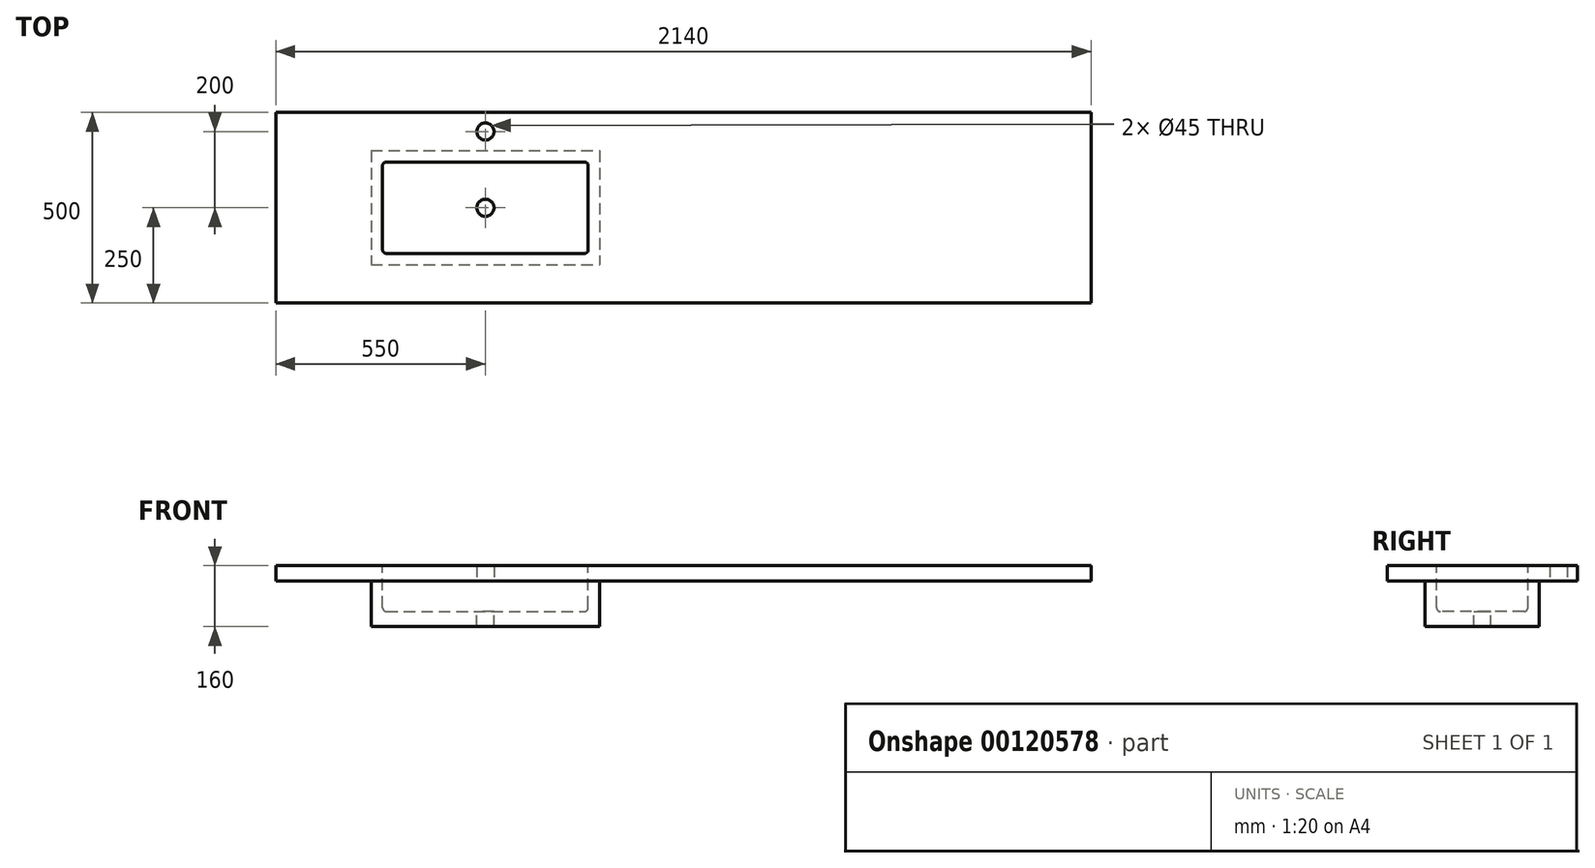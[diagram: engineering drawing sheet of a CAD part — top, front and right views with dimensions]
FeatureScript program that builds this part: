
annotation { "Feature Type Name" : "Feature", "Feature Type Description" : "" }
export const myFeature = defineFeature(function(context is Context, id is Id, definition is map)
    precondition{}
    {
        {
            var Q0;
            Q0=qCreatedBy(makeId("Top.planeOp"),FACE);
            var sketch = newSketch(context, id + "F0", { "sketchPlane" : qUnion([Q0])});
            skLineSegment(sketch, "E0.bottom", {"start": v(1070, 250) * mm, "end": v(-1070, 250) * mm});
            skLineSegment(sketch, "E0.top", {"start": v(1070, -250) * mm, "end": v(-1070, -250) * mm});
            skLineSegment(sketch, "E0.left", {"start": v(1070, 250) * mm, "end": v(1070, -250) * mm});
            skLineSegment(sketch, "E0.right", {"start": v(-1070, 250) * mm, "end": v(-1070, -250) * mm});
            skPoint(sketch, "E0.middle", {"position": v(0, 0) * mm});
            skSolve(sketch);
        }
        {
            var Q0;
            Q0 = qSketchRegion(id + "F0", true);
            extrude(context, id + "F1", {"entities" : qUnion([Q0]), "depth" : 40 * mm, "offsetDistance" : 25 * mm});
        }
        {
            var Q0;
            Q0=makeQuery(id+"F1.opExtrude","CAP_FACE",FACE,{"disambiguationData":[OSD([sQuery(id+"F0.wireOp",EDGE,"E0.bottom"),sQuery(id+"F0.wireOp",EDGE,"E0.top"),sQuery(id+"F0.wireOp",EDGE,"E0.left"),sQuery(id+"F0.wireOp",EDGE,"E0.right")])],"isStart":true});
            var sketch = newSketch(context, id + "F2", { "sketchPlane" : qUnion([Q0])});
            skLineSegment(sketch, "E1.bottom", {"start": v(-820, -150) * mm, "end": v(-220, -150) * mm});
            skLineSegment(sketch, "E1.top", {"start": v(-820, 150) * mm, "end": v(-220, 150) * mm});
            skLineSegment(sketch, "E1.left", {"start": v(-820, -150) * mm, "end": v(-820, 150) * mm});
            skLineSegment(sketch, "E1.right", {"start": v(-220, -150) * mm, "end": v(-220, 150) * mm});
            skLineSegment(sketch, "E2", {"start": v(-820, 0) * mm, "end": v(-1070, 0) * mm, "construction": true});
            skSolve(sketch);
        }
        {
            var Q0;
            Q0=makeQuery(id+"F2.imprint","IMPRINT",FACE,{"disambiguationData":[TD([[makeQuery(id+"F2.imprint","IMPRINT",EDGE,{"derivedFrom":sQuery(id+"F2.wireOp",EDGE,"E1.bottom")}),1.0]])]});
            extrude(context, id + "F3", {"entities" : qUnion([Q0]), "operationType" : NewBodyOperationType.ADD, "depth" : 120 * mm, "offsetDistance" : 25 * mm});
        }
        {
            var Q0;
            Q0=makeQuery(id+"F1.opExtrude","CAP_FACE",FACE,{"disambiguationData":[OSD([sQuery(id+"F0.wireOp",EDGE,"E0.bottom"),sQuery(id+"F0.wireOp",EDGE,"E0.top"),sQuery(id+"F0.wireOp",EDGE,"E0.left"),sQuery(id+"F0.wireOp",EDGE,"E0.right")])],"isStart":true});
            var sketch = newSketch(context, id + "F4", { "sketchPlane" : qUnion([Q0])});
            skCircle(sketch, "E3", {"center": v(-520, -200) * mm, "radius": 20 * mm});
            skLineSegment(sketch, "E4", {"start": v(-520, -200) * mm, "end": v(-520, -150) * mm});
            skSolve(sketch);
        }
        {
            var Q0;
            Q0=sQuery(id+"F4.wireOp",VERTEX,"E3.center");
            var Q1;
            Q1=makeQuery(id+"F1.opExtrude","SWEPT_BODY",BODY,{"disambiguationData":[OSD([sQuery(id+"F0.wireOp",EDGE,"E0.bottom"),sQuery(id+"F0.wireOp",EDGE,"E0.top"),sQuery(id+"F0.wireOp",EDGE,"E0.left"),sQuery(id+"F0.wireOp",EDGE,"E0.right")])]});
            hole(context, id + "F5", {"style" : HoleStyle.SIMPLE, "endStyle" : HoleEndStyle.THROUGH, "holeDiameter" : 45 * mm, "locations" : qUnion([Q0]), "scope" : qUnion([Q1]), "majorDiameter" : 5 * mm, "tappedDepth" : 12 * mm, "tapClearance" : 3});
        }
        {
            var Q0;
            Q0=makeQuery(id+"F1.opExtrude","CAP_FACE",FACE,{"disambiguationData":[OSD([sQuery(id+"F0.wireOp",EDGE,"E0.bottom"),sQuery(id+"F0.wireOp",EDGE,"E0.top"),sQuery(id+"F0.wireOp",EDGE,"E0.left"),sQuery(id+"F0.wireOp",EDGE,"E0.right")])],"isStart":false});
            var sketch = newSketch(context, id + "F6", { "sketchPlane" : qUnion([Q0])});
            skLineSegment(sketch, "E5.0.0", {"start": v(-220, -150) * mm, "end": v(-820, -150) * mm});
            skLineSegment(sketch, "E5.0.1", {"start": v(-820, -150) * mm, "end": v(-820, 150) * mm});
            skLineSegment(sketch, "E5.0.2", {"start": v(-820, 150) * mm, "end": v(-220, 150) * mm});
            skLineSegment(sketch, "E5.0.3", {"start": v(-220, 150) * mm, "end": v(-220, -150) * mm});
            skLineSegment(sketch, "E6.0", {"start": v(-250, -120) * mm, "end": v(-790, -120) * mm});
            skLineSegment(sketch, "E6.1", {"start": v(-250, 120) * mm, "end": v(-250, -120) * mm});
            skLineSegment(sketch, "E6.2", {"start": v(-790, 120) * mm, "end": v(-250, 120) * mm});
            skLineSegment(sketch, "E6.3", {"start": v(-790, -120) * mm, "end": v(-790, 120) * mm});
            skSolve(sketch);
        }
        {
            var Q0;
            Q0=makeQuery(id+"F6.imprint","IMPRINT",FACE,{"disambiguationData":[TD([[makeQuery(id+"F6.imprint","IMPRINT",EDGE,{"derivedFrom":sQuery(id+"F6.wireOp",EDGE,"E6.0")}),-1.0]])]});
            extrude(context, id + "F7", {"entities" : qUnion([Q0]), "operationType" : NewBodyOperationType.REMOVE, "oppositeDirection" : true, "depth" : 120 * mm, "offsetDistance" : 25 * mm});
        }
        {
            var Q0;
            Q0=makeQuery(id+"F7.boolean.opBoolean","COPY",EDGE,{"derivedFrom":makeQuery(id+"F7.opExtrude","SWEPT_EDGE",EDGE,{"disambiguationData":[OSD([sQuery(id+"F6.wireOp",EDGE,"E6.0"),sQuery(id+"F6.wireOp",EDGE,"E6.1")])]})});
            var Q1;
            Q1=makeQuery(id+"F7.boolean.opBoolean","COPY",EDGE,{"derivedFrom":makeQuery(id+"F7.opExtrude","CAP_EDGE",EDGE,{"disambiguationData":[OSD([sQuery(id+"F6.wireOp",EDGE,"E6.1")])],"isStart":false})});
            var Q2;
            Q2=makeQuery(id+"F7.boolean.opBoolean","COPY",EDGE,{"derivedFrom":makeQuery(id+"F7.opExtrude","CAP_EDGE",EDGE,{"disambiguationData":[OSD([sQuery(id+"F6.wireOp",EDGE,"E6.0")])],"isStart":false})});
            var Q3;
            Q3=makeQuery(id+"F7.boolean.opBoolean","COPY",EDGE,{"derivedFrom":makeQuery(id+"F7.opExtrude","SWEPT_EDGE",EDGE,{"disambiguationData":[OSD([sQuery(id+"F6.wireOp",EDGE,"E6.0"),sQuery(id+"F6.wireOp",EDGE,"E6.3")])]})});
            var Q4;
            Q4=makeQuery(id+"F7.boolean.opBoolean","COPY",EDGE,{"derivedFrom":makeQuery(id+"F7.opExtrude","CAP_EDGE",EDGE,{"disambiguationData":[OSD([sQuery(id+"F6.wireOp",EDGE,"E6.3")])],"isStart":false})});
            var Q5;
            Q5=makeQuery(id+"F7.boolean.opBoolean","COPY",EDGE,{"derivedFrom":makeQuery(id+"F7.opExtrude","CAP_EDGE",EDGE,{"disambiguationData":[OSD([sQuery(id+"F6.wireOp",EDGE,"E6.2")])],"isStart":false})});
            var Q6;
            Q6=makeQuery(id+"F7.boolean.opBoolean","COPY",EDGE,{"derivedFrom":makeQuery(id+"F7.opExtrude","SWEPT_EDGE",EDGE,{"disambiguationData":[OSD([sQuery(id+"F6.wireOp",EDGE,"E6.1"),sQuery(id+"F6.wireOp",EDGE,"E6.2")])]})});
            var Q7;
            Q7=makeQuery(id+"F7.boolean.opBoolean","COPY",EDGE,{"derivedFrom":makeQuery(id+"F7.opExtrude","SWEPT_EDGE",EDGE,{"disambiguationData":[OSD([sQuery(id+"F6.wireOp",EDGE,"E6.2"),sQuery(id+"F6.wireOp",EDGE,"E6.3")])]})});
            fillet(context, id + "F8", {"entities" : qUnion([Q0, Q1, Q2, Q3, Q4, Q5, Q6, Q7]), "radius" : 10 * mm, "tangentPropagation" : true, "allowEdgeOverflow" : false});
        }
        {
            var Q0;
            Q0=makeQuery(id+"F7.boolean.opBoolean","COPY",FACE,{"derivedFrom":makeQuery(id+"F7.opExtrude","CAP_FACE",FACE,{"disambiguationData":[OSD([sQuery(id+"F6.wireOp",EDGE,"E6.0"),sQuery(id+"F6.wireOp",EDGE,"E6.1"),sQuery(id+"F6.wireOp",EDGE,"E6.2"),sQuery(id+"F6.wireOp",EDGE,"E6.3")])],"isStart":false})});
            var sketch = newSketch(context, id + "F9", { "sketchPlane" : qUnion([Q0])});
            skPoint(sketch, "E7", {"position": v(-520, 0) * mm});
            skPoint(sketch, "E7.positionSnap0", {"position": v(-780, 0) * mm});
            skPoint(sketch, "E7.positionSnap1", {"position": v(-520, 110) * mm});
            skSolve(sketch);
        }
        {
            var Q0;
            Q0=sQuery(id+"F9.wireOp",VERTEX,"E7");
            var Q1;
            Q1=makeQuery(id+"F1.opExtrude","SWEPT_BODY",BODY,{"disambiguationData":[OSD([sQuery(id+"F0.wireOp",EDGE,"E0.bottom"),sQuery(id+"F0.wireOp",EDGE,"E0.top"),sQuery(id+"F0.wireOp",EDGE,"E0.left"),sQuery(id+"F0.wireOp",EDGE,"E0.right")])]});
            hole(context, id + "F10", {"style" : HoleStyle.SIMPLE, "endStyle" : HoleEndStyle.THROUGH, "holeDiameter" : 45 * mm, "majorDiameter" : 5 * mm, "tappedDepth" : 12 * mm, "tapClearance" : 3, "locations" : qUnion([Q0]), "scope" : qUnion([Q1])});
        }
    });
